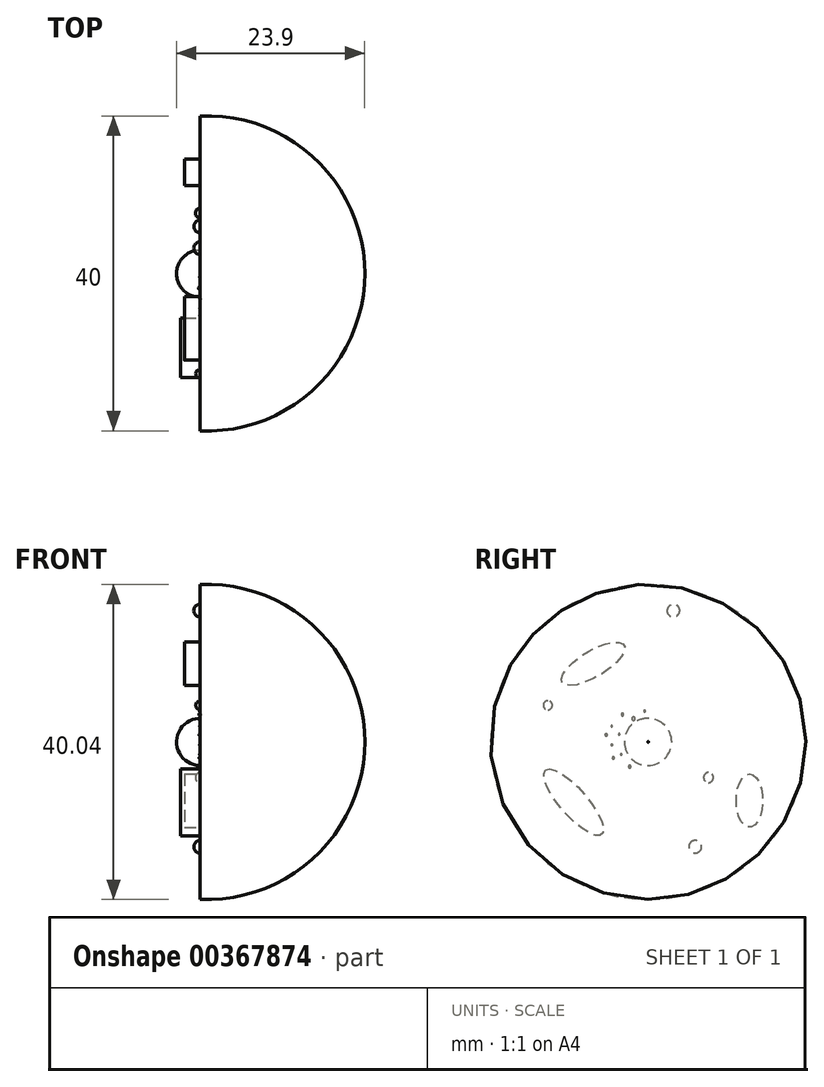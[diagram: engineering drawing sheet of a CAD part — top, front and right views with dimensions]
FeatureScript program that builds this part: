
annotation { "Feature Type Name" : "Feature", "Feature Type Description" : "" }
export const myFeature = defineFeature(function(context is Context, id is Id, definition is map)
    precondition{}
    {
        {
            var Q0;
            Q0=qCreatedBy(makeId("Front.planeOp"),FACE);
            var sketch = newSketch(context, id + "F0", { "sketchPlane" : qUnion([Q0])});
            skLineSegment(sketch, "E0", {"start": v(0, 0) * mm, "end": v(0, 20) * mm});
            skLineSegment(sketch, "E1", {"start": v(0, 0) * mm, "end": v(20.9, 0) * mm});
            skArc(sketch, "E2", {"start": v(20.9, 0) * mm, "mid": v(14.71, 14.46) * mm, "end": v(0, 20) * mm});
            skSolve(sketch);
        }
        {
            var Q0;
            Q0=makeQuery(id+"F0.imprint","IMPRINT",FACE,{"disambiguationData":[TD([[makeQuery(id+"F0.imprint","IMPRINT",EDGE,{"derivedFrom":sQuery(id+"F0.wireOp",EDGE,"E0")}),-1.0]])]});
            var Q1;
            Q1=sQuery(id+"F0.wireOp",EDGE,"E1");
            revolve(context, id + "F1", {"entities" : qUnion([Q0]), "axis" : qUnion([Q1]), "revolveType" : RevolveType.FULL});
        }
        {
            var Q0;
            Q0=qCreatedBy(makeId("Right.planeOp"),FACE);
            var sketch = newSketch(context, id + "F2", { "sketchPlane" : qUnion([Q0])});
            skLineSegment(sketch, "E3", {"start": v(0, 0) * mm, "end": v(0, 3) * mm});
            skLineSegment(sketch, "E4", {"start": v(0, 0) * mm, "end": v(-3, 0) * mm});
            skArc(sketch, "E5", {"start": v(0, 3) * mm, "mid": v(-2.14, 2.14) * mm, "end": v(-3, 0) * mm});
            skSolve(sketch);
        }
        {
            var Q0;
            Q0 = qSketchRegion(id + "F2", true);
            var Q1;
            Q1=sQuery(id+"F2.wireOp",EDGE,"E4");
            revolve(context, id + "F3", {"operationType" : NewBodyOperationType.ADD, "entities" : qUnion([Q0]), "axis" : qUnion([Q1]), "revolveType" : RevolveType.FULL});
        }
        {
            var Q0;
            Q0=makeQuery(id+"F1.opRevolve","SWEPT_FACE",FACE,{"disambiguationData":[OSD([sQuery(id+"F0.wireOp",EDGE,"E0")])]});
            var sketch = newSketch(context, id + "F4", { "sketchPlane" : qUnion([Q0])});
            skLineSegment(sketch, "E6", {"start": v(0, 0) * mm, "end": v(-3, 0) * mm});
            skLineSegment(sketch, "E7", {"start": v(0, 0) * mm, "end": v(0, 3) * mm});
            skArc(sketch, "E8", {"start": v(0, 3) * mm, "mid": v(-2.1, 2.1) * mm, "end": v(-3, 0) * mm});
            skSolve(sketch);
        }
        {
            var Q0;
            Q0=makeQuery(id+"F4.imprint","IMPRINT",FACE,{"disambiguationData":[TD([[makeQuery(id+"F4.imprint","IMPRINT",EDGE,{"derivedFrom":sQuery(id+"F4.wireOp",EDGE,"E6")}),-1.0]])]});
            var Q1;
            Q1=sQuery(id+"F4.wireOp",EDGE,"E6");
            revolve(context, id + "F5", {"operationType" : NewBodyOperationType.ADD, "entities" : qUnion([Q0]), "axis" : qUnion([Q1]), "revolveType" : RevolveType.FULL});
        }
        {
            var Q0;
            Q0=makeQuery(id+"F1.opRevolve","SWEPT_FACE",FACE,{"disambiguationData":[OSD([sQuery(id+"F0.wireOp",EDGE,"E0")])]});
            var sketch = newSketch(context, id + "F6", { "sketchPlane" : qUnion([Q0])});
            skEllipse(sketch, "E9", {"center": v(9.46, -7.67) * mm, "majorRadius": 5.42 * mm, "minorRadius": 1.7 * mm, "majorAxis": v(0.66, 0.75)});
            skSolve(sketch);
        }
        {
            var Q0;
            Q0 = qSketchRegion(id + "F6", true);
            extrude(context, id + "F7", {"entities" : qUnion([Q0]), "depth" : 2.5 * mm});
        }
        {
            var Q0;
            Q0=makeQuery(id+"F7.opExtrude","CAP_FACE",FACE,{"disambiguationData":[OSD([sQuery(id+"F6.wireOp",EDGE,"E9")])],"isStart":false});
            var sketch = newSketch(context, id + "F8", { "sketchPlane" : qUnion([Q0])});
            skFitSpline(sketch, "E10", {"points": [v(7.97, -11.28) * mm, v(6.8, -8.9) * mm, v(9.38, -10.19) * mm, v(8.17, -7.24) * mm, v(11, -8.49) * mm, v(9.27, -5.4) * mm, v(11.92, -6.7) * mm, v(11.05, -4) * mm, v(13.1, -5.01) * mm], "startDerivative": vector(-20.7, 30.85) * mm, "endDerivative": vector(27.66, -19.9) * mm});
            skSolve(sketch);
        }
        {
            var Q0;
            Q0 = qSketchRegion(id + "F8", true);
            var Q1;
            Q1=sQuery(id+"F8.wireOp",EDGE,"E10");
            extrude(context, id + "F9", {"entities" : qUnion([Q0]), "bodyType" : ToolBodyType.SURFACE, "surfaceEntities" : qUnion([Q1]), "oppositeDirection" : true, "depth" : 2 * mm});
        }
        {
            var Q0;
            Q0=makeQuery(id+"F1.opRevolve","SWEPT_FACE",FACE,{"disambiguationData":[OSD([sQuery(id+"F0.wireOp",EDGE,"E0")])]});
            var sketch = newSketch(context, id + "F10", { "sketchPlane" : qUnion([Q0])});
            skSolve(sketch);
        }
        {
            var Q0;
            {var subQ1=sQuery(id+"F0.wireOp",EDGE,"E0");Q0=makeQuery(id+"F10.imprint","IMPRINT",FACE,{"disambiguationData":[TD([[makeQuery(id+"F10.imprint","IMPRINT",EDGE,{"derivedFrom":makeQuery(id+"F1.opRevolve","SWEPT_EDGE",EDGE,{"disambiguationData":[OSD([subQ1,sQuery(id+"F0.wireOp",EDGE,"E2")])]})}),1.0]])]});}
            var sketch = newSketch(context, id + "F11", { "sketchPlane" : qUnion([Q0])});
            skSolve(sketch);
        }
        {
            var Q0;
            {var subQ1=sQuery(id+"F0.wireOp",EDGE,"E0");Q0=makeQuery(id+"F10.imprint","IMPRINT",FACE,{"disambiguationData":[TD([[makeQuery(id+"F10.imprint","IMPRINT",EDGE,{"derivedFrom":makeQuery(id+"F1.opRevolve","SWEPT_EDGE",EDGE,{"disambiguationData":[OSD([subQ1,sQuery(id+"F0.wireOp",EDGE,"E2")])]})}),1.0]])]});}
            var sketch = newSketch(context, id + "F12", { "sketchPlane" : qUnion([Q0])});
            skEllipse(sketch, "E11", {"center": v(6.98, 9.93) * mm, "majorRadius": 4.6 * mm, "minorRadius": 1.66 * mm, "majorAxis": v(0.86, -0.51)});
            skSolve(sketch);
        }
        {
            var Q0;
            Q0 = qSketchRegion(id + "F12", true);
            extrude(context, id + "F13", {"entities" : qUnion([Q0]), "depth" : 2 * mm});
        }
        {
            var Q0;
            Q0=makeQuery(id+"F13.opExtrude","CAP_FACE",FACE,{"disambiguationData":[OSD([sQuery(id+"F12.wireOp",EDGE,"E11")])],"isStart":false});
            var sketch = newSketch(context, id + "F14", { "sketchPlane" : qUnion([Q0])});
            skFitSpline(sketch, "E12", {"points": [v(4.68, 12.63) * mm, v(3.63, 10.54) * mm, v(6.2, 12.18) * mm, v(5.11, 9.18) * mm, v(7.84, 11.35) * mm, v(6.92, 8.06) * mm, v(9.45, 10.2) * mm, v(9.08, 7.26) * mm], "startDerivative": vector(-17.32, -26.87) * mm, "endDerivative": vector(-10.03, -33.63) * mm});
            skSolve(sketch);
        }
        {
            var Q0;
            Q0 = qSketchRegion(id + "F14", true);
            var Q1;
            Q1=sQuery(id+"F14.wireOp",EDGE,"E12");
            extrude(context, id + "F15", {"entities" : qUnion([Q0]), "bodyType" : ToolBodyType.SURFACE, "surfaceEntities" : qUnion([Q1]), "oppositeDirection" : true, "depth" : 2 * mm});
        }
        {
            var Q0;
            {var subQ1=sQuery(id+"F0.wireOp",EDGE,"E0");Q0=makeQuery(id+"F10.imprint","IMPRINT",FACE,{"disambiguationData":[TD([[makeQuery(id+"F10.imprint","IMPRINT",EDGE,{"derivedFrom":makeQuery(id+"F1.opRevolve","SWEPT_EDGE",EDGE,{"disambiguationData":[OSD([subQ1,sQuery(id+"F0.wireOp",EDGE,"E2")])]})}),1.0]])]});}
            var sketch = newSketch(context, id + "F16", { "sketchPlane" : qUnion([Q0])});
            skFitSpline(sketch, "E13", {"points": [v(-13.4, 3.83) * mm, v(-13, 6.76) * mm, v(-11.02, 11.05) * mm, v(-7.06, 13.56) * mm, v(-3.83, 13.87) * mm, v(-2.72, 12.84) * mm, v(-4.78, 12.22) * mm, v(-7.76, 11.16) * mm, v(-9.8, 9.35) * mm, v(-10.94, 6.79) * mm, v(-11.41, 3.75) * mm, v(-10.83, 2.72) * mm, v(-9.4, 6.15) * mm, v(-7.32, 9.32) * mm, v(-3.78, 10.86) * mm, v(-3.25, 8.93) * mm, v(-5.3, 8.35) * mm, v(-7.26, 6.9) * mm, v(-8.35, 4.25) * mm, v(-7.57, 3.02) * mm, v(-6.48, 4.95) * mm, v(-5.4, 6.65) * mm, v(-2.94, 7.46) * mm, v(-2.5, 6.23) * mm, v(-4.8, 5.59) * mm, v(-6.14, 2.41) * mm], "startDerivative": vector(4.96, 65.1) * mm, "endDerivative": vector(-14.45, -88.75) * mm});
            skSolve(sketch);
        }
        {
            var Q0;
            Q0 = qSketchRegion(id + "F16", true);
            var Q1;
            Q1=sQuery(id+"F16.wireOp",EDGE,"E13");
            extrude(context, id + "F17", {"entities" : qUnion([Q0]), "bodyType" : ToolBodyType.SURFACE, "surfaceEntities" : qUnion([Q1]), "depth" : 2 * mm});
        }
        {
            var Q0;
            {var subQ1=sQuery(id+"F0.wireOp",EDGE,"E0");Q0=makeQuery(id+"F10.imprint","IMPRINT",FACE,{"disambiguationData":[TD([[makeQuery(id+"F10.imprint","IMPRINT",EDGE,{"derivedFrom":makeQuery(id+"F1.opRevolve","SWEPT_EDGE",EDGE,{"disambiguationData":[OSD([subQ1,sQuery(id+"F0.wireOp",EDGE,"E2")])]})}),1.0]])]});}
            var sketch = newSketch(context, id + "F18", { "sketchPlane" : qUnion([Q0])});
            skFitSpline(sketch, "E14", {"points": [v(1.63, 7.11) * mm, v(4.78, 6.86) * mm, v(8.1, 5.2) * mm, v(9.66, 1.11) * mm, v(8.41, -3.01) * mm, v(4.67, -6.66) * mm, v(1.55, -7.21) * mm, v(1.07, -5.9) * mm, v(5.1, -4.45) * mm, v(7.63, -0.85) * mm, v(7.17, 3.33) * mm, v(4.59, 5.28) * mm, v(0, 5.94) * mm, v(0, 5.08) * mm, v(3.24, 4.42) * mm, v(5.82, 2.74) * mm, v(6.18, 0) * mm, v(5.56, -2.02) * mm, v(3.12, -3.79) * mm, v(1.15, -4.12) * mm, v(1.1, -3.42) * mm, v(3.12, -2.7) * mm, v(4.9, -0.76) * mm, v(4.7, 2.17) * mm, v(3.65, 3.54) * mm, v(1.42, 3.89) * mm, v(0, 3.94) * mm, v(0, 3.36) * mm, v(2.32, 3.19) * mm, v(3.68, 1.68) * mm, v(3.9, 0) * mm, v(3.27, -1.54) * mm, v(2.16, -2.36) * mm], "startDerivative": vector(88.94, -1.16) * mm, "endDerivative": vector(-52.62, -29.6) * mm});
            skSolve(sketch);
        }
        {
            var Q0;
            Q0 = qSketchRegion(id + "F18", true);
            var Q1;
            Q1=sQuery(id+"F18.wireOp",EDGE,"E14");
            extrude(context, id + "F19", {"entities" : qUnion([Q0]), "bodyType" : ToolBodyType.SURFACE, "surfaceEntities" : qUnion([Q1]), "depth" : 1.8 * mm});
        }
        {
            var Q0;
            {var subQ1=sQuery(id+"F0.wireOp",EDGE,"E0");Q0=makeQuery(id+"F10.imprint","IMPRINT",FACE,{"disambiguationData":[TD([[makeQuery(id+"F10.imprint","IMPRINT",EDGE,{"derivedFrom":makeQuery(id+"F1.opRevolve","SWEPT_EDGE",EDGE,{"disambiguationData":[OSD([subQ1,sQuery(id+"F0.wireOp",EDGE,"E2")])]})}),1.0]])]});}
            var sketch = newSketch(context, id + "F20", { "sketchPlane" : qUnion([Q0])});
            skLineSegment(sketch, "E15", {"start": v(-7.66, -5.18) * mm, "end": v(-7.66, -3.88) * mm});
            skArc(sketch, "E16", {"start": v(-7.66, -3.88) * mm, "mid": v(-8.27, -4.53) * mm, "end": v(-7.66, -5.18) * mm});
            skSolve(sketch);
        }
        {
            var Q0;
            Q0 = qSketchRegion(id + "F20", true);
            var Q1;
            Q1=sQuery(id+"F20.wireOp",EDGE,"E15");
            revolve(context, id + "F21", {"operationType" : NewBodyOperationType.ADD, "entities" : qUnion([Q0]), "axis" : qUnion([Q1]), "revolveType" : RevolveType.FULL});
        }
        {
            var Q0;
            {var subQ1=sQuery(id+"F0.wireOp",EDGE,"E0");Q0=makeQuery(id+"F10.imprint","IMPRINT",FACE,{"disambiguationData":[TD([[makeQuery(id+"F10.imprint","IMPRINT",EDGE,{"derivedFrom":makeQuery(id+"F1.opRevolve","SWEPT_EDGE",EDGE,{"disambiguationData":[OSD([subQ1,sQuery(id+"F0.wireOp",EDGE,"E2")])]})}),1.0]])]});}
            var sketch = newSketch(context, id + "F22", { "sketchPlane" : qUnion([Q0])});
            skLineSegment(sketch, "E17", {"start": v(12.74, 4.08) * mm, "end": v(12.74, 5.23) * mm});
            skArc(sketch, "E18", {"start": v(12.74, 5.23) * mm, "mid": v(12.17, 4.66) * mm, "end": v(12.74, 4.08) * mm});
            skSolve(sketch);
        }
        {
            var Q0;
            Q0 = qSketchRegion(id + "F22", true);
            var Q1;
            Q1=sQuery(id+"F22.wireOp",EDGE,"E17");
            revolve(context, id + "F23", {"operationType" : NewBodyOperationType.ADD, "entities" : qUnion([Q0]), "axis" : qUnion([Q1]), "revolveType" : RevolveType.FULL});
        }
        {
            var Q0;
            {var subQ1=sQuery(id+"F0.wireOp",EDGE,"E0");Q0=makeQuery(id+"F10.imprint","IMPRINT",FACE,{"disambiguationData":[TD([[makeQuery(id+"F10.imprint","IMPRINT",EDGE,{"derivedFrom":makeQuery(id+"F1.opRevolve","SWEPT_EDGE",EDGE,{"disambiguationData":[OSD([subQ1,sQuery(id+"F0.wireOp",EDGE,"E2")])]})}),1.0]])]});}
            var sketch = newSketch(context, id + "F24", { "sketchPlane" : qUnion([Q0])});
            skLineSegment(sketch, "E19", {"start": v(-5.97, -14.13) * mm, "end": v(-5.97, -12.52) * mm});
            skArc(sketch, "E20", {"start": v(-5.97, -12.52) * mm, "mid": v(-6.78, -13.33) * mm, "end": v(-5.97, -14.13) * mm});
            skSolve(sketch);
        }
        {
            var Q0;
            Q0 = qSketchRegion(id + "F24", true);
            var Q1;
            Q1=sQuery(id+"F24.wireOp",EDGE,"E19");
            revolve(context, id + "F25", {"operationType" : NewBodyOperationType.ADD, "entities" : qUnion([Q0]), "axis" : qUnion([Q1]), "revolveType" : RevolveType.FULL});
        }
        {
            var Q0;
            {var subQ1=sQuery(id+"F0.wireOp",EDGE,"E0");Q0=makeQuery(id+"F10.imprint","IMPRINT",FACE,{"disambiguationData":[TD([[makeQuery(id+"F10.imprint","IMPRINT",EDGE,{"derivedFrom":makeQuery(id+"F1.opRevolve","SWEPT_EDGE",EDGE,{"disambiguationData":[OSD([subQ1,sQuery(id+"F0.wireOp",EDGE,"E2")])]})}),1.0]])]});}
            var sketch = newSketch(context, id + "F26", { "sketchPlane" : qUnion([Q0])});
            skLineSegment(sketch, "E21", {"start": v(-3.75, 16.1) * mm, "end": v(-2.67, 17.25) * mm});
            skArc(sketch, "E22", {"start": v(-2.67, 17.25) * mm, "mid": v(-3.8, 17.24) * mm, "end": v(-3.75, 16.1) * mm});
            skSolve(sketch);
        }
        {
            var Q0;
            Q0 = qSketchRegion(id + "F26", true);
            var Q1;
            Q1=sQuery(id+"F26.wireOp",EDGE,"E21");
            revolve(context, id + "F27", {"operationType" : NewBodyOperationType.ADD, "entities" : qUnion([Q0]), "axis" : qUnion([Q1]), "revolveType" : RevolveType.FULL});
        }
        {
            var Q0;
            {var subQ1=sQuery(id+"F0.wireOp",EDGE,"E0");Q0=makeQuery(id+"F10.imprint","IMPRINT",FACE,{"disambiguationData":[TD([[makeQuery(id+"F10.imprint","IMPRINT",EDGE,{"derivedFrom":makeQuery(id+"F1.opRevolve","SWEPT_EDGE",EDGE,{"disambiguationData":[OSD([subQ1,sQuery(id+"F0.wireOp",EDGE,"E2")])]})}),1.0]])]});}
            var sketch = newSketch(context, id + "F28", { "sketchPlane" : qUnion([Q0])});
            skLineSegment(sketch, "E23", {"start": v(3.12, 3.49) * mm, "end": v(3.4, 3.49) * mm});
            skArc(sketch, "E24", {"start": v(3.4, 3.49) * mm, "mid": v(3.26, 3.61) * mm, "end": v(3.12, 3.49) * mm});
            skSolve(sketch);
        }
        {
            var Q0;
            Q0 = qSketchRegion(id + "F28", true);
            var Q1;
            Q1=sQuery(id+"F28.wireOp",EDGE,"E23");
            revolve(context, id + "F29", {"entities" : qUnion([Q0]), "axis" : qUnion([Q1]), "revolveType" : RevolveType.FULL});
        }
        {
            var Q0;
            {var subQ1=sQuery(id+"F0.wireOp",EDGE,"E0");Q0=makeQuery(id+"F10.imprint","IMPRINT",FACE,{"disambiguationData":[TD([[makeQuery(id+"F10.imprint","IMPRINT",EDGE,{"derivedFrom":makeQuery(id+"F1.opRevolve","SWEPT_EDGE",EDGE,{"disambiguationData":[OSD([subQ1,sQuery(id+"F0.wireOp",EDGE,"E2")])]})}),1.0]])]});}
            var sketch = newSketch(context, id + "F30", { "sketchPlane" : qUnion([Q0])});
            skLineSegment(sketch, "E25", {"start": v(1.66, 2.96) * mm, "end": v(2.07, 2.96) * mm});
            skArc(sketch, "E26", {"start": v(2.07, 2.96) * mm, "mid": v(1.86, 3.17) * mm, "end": v(1.66, 2.96) * mm});
            skSolve(sketch);
        }
        {
            var Q0;
            Q0 = qSketchRegion(id + "F30", true);
            var Q1;
            Q1=sQuery(id+"F30.wireOp",EDGE,"E25");
            revolve(context, id + "F31", {"operationType" : NewBodyOperationType.ADD, "entities" : qUnion([Q0]), "axis" : qUnion([Q1]), "revolveType" : RevolveType.FULL});
        }
        {
            var Q0;
            {var subQ1=sQuery(id+"F0.wireOp",EDGE,"E0");Q0=makeQuery(id+"F10.imprint","IMPRINT",FACE,{"disambiguationData":[TD([[makeQuery(id+"F10.imprint","IMPRINT",EDGE,{"derivedFrom":makeQuery(id+"F1.opRevolve","SWEPT_EDGE",EDGE,{"disambiguationData":[OSD([subQ1,sQuery(id+"F0.wireOp",EDGE,"E2")])]})}),1.0]])]});}
            var sketch = newSketch(context, id + "F32", { "sketchPlane" : qUnion([Q0])});
            skLineSegment(sketch, "E27", {"start": v(4.55, 2) * mm, "end": v(4.73, 2) * mm});
            skArc(sketch, "E28", {"start": v(4.73, 2) * mm, "mid": v(4.64, 2.07) * mm, "end": v(4.55, 2) * mm});
            skSolve(sketch);
        }
        {
            var Q0;
            Q0 = qSketchRegion(id + "F32", true);
            var Q1;
            Q1=sQuery(id+"F32.wireOp",EDGE,"E27");
            revolve(context, id + "F33", {"operationType" : NewBodyOperationType.ADD, "entities" : qUnion([Q0]), "axis" : qUnion([Q1]), "revolveType" : RevolveType.FULL});
        }
        {
            var Q0;
            {var subQ1=sQuery(id+"F0.wireOp",EDGE,"E0");Q0=makeQuery(id+"F10.imprint","IMPRINT",FACE,{"disambiguationData":[TD([[makeQuery(id+"F10.imprint","IMPRINT",EDGE,{"derivedFrom":makeQuery(id+"F1.opRevolve","SWEPT_EDGE",EDGE,{"disambiguationData":[OSD([subQ1,sQuery(id+"F0.wireOp",EDGE,"E2")])]})}),1.0]])]});}
            var sketch = newSketch(context, id + "F34", { "sketchPlane" : qUnion([Q0])});
            skLineSegment(sketch, "E29", {"start": v(4.5, -0.38) * mm, "end": v(4.7, -0.38) * mm});
            skArc(sketch, "E30", {"start": v(4.5, -0.38) * mm, "mid": v(4.6, -0.48) * mm, "end": v(4.7, -0.38) * mm});
            skSolve(sketch);
        }
        {
            var Q0;
            Q0 = qSketchRegion(id + "F34", true);
            var Q1;
            Q1=sQuery(id+"F34.wireOp",EDGE,"E29");
            revolve(context, id + "F35", {"operationType" : NewBodyOperationType.ADD, "entities" : qUnion([Q0]), "axis" : qUnion([Q1]), "revolveType" : RevolveType.FULL});
        }
        {
            var Q0;
            {var subQ1=sQuery(id+"F0.wireOp",EDGE,"E0");Q0=makeQuery(id+"F10.imprint","IMPRINT",FACE,{"disambiguationData":[TD([[makeQuery(id+"F10.imprint","IMPRINT",EDGE,{"derivedFrom":makeQuery(id+"F1.opRevolve","SWEPT_EDGE",EDGE,{"disambiguationData":[OSD([subQ1,sQuery(id+"F0.wireOp",EDGE,"E2")])]})}),1.0]])]});}
            var sketch = newSketch(context, id + "F36", { "sketchPlane" : qUnion([Q0])});
            skLineSegment(sketch, "E31", {"start": v(2.2, -3.15) * mm, "end": v(2.49, -3.15) * mm});
            skArc(sketch, "E32", {"start": v(2.49, -3.15) * mm, "mid": v(2.34, -3) * mm, "end": v(2.2, -3.15) * mm});
            skSolve(sketch);
        }
        {
            var Q0;
            Q0 = qSketchRegion(id + "F36", true);
            var Q1;
            Q1=sQuery(id+"F36.wireOp",EDGE,"E31");
            revolve(context, id + "F37", {"operationType" : NewBodyOperationType.ADD, "entities" : qUnion([Q0]), "axis" : qUnion([Q1]), "revolveType" : RevolveType.FULL});
        }
        {
            var Q0;
            {var subQ1=sQuery(id+"F0.wireOp",EDGE,"E0");Q0=makeQuery(id+"F10.imprint","IMPRINT",FACE,{"disambiguationData":[TD([[makeQuery(id+"F10.imprint","IMPRINT",EDGE,{"derivedFrom":makeQuery(id+"F1.opRevolve","SWEPT_EDGE",EDGE,{"disambiguationData":[OSD([subQ1,sQuery(id+"F0.wireOp",EDGE,"E2")])]})}),1.0]])]});}
            var sketch = newSketch(context, id + "F38", { "sketchPlane" : qUnion([Q0])});
            skLineSegment(sketch, "E33", {"start": v(3.6, 0.96) * mm, "end": v(3.78, 0.96) * mm});
            skArc(sketch, "E34", {"start": v(3.78, 0.96) * mm, "mid": v(3.7, 1.05) * mm, "end": v(3.6, 0.96) * mm});
            skSolve(sketch);
        }
        {
            var Q0;
            Q0 = qSketchRegion(id + "F38", true);
            var Q1;
            Q1=sQuery(id+"F38.wireOp",EDGE,"E33");
            revolve(context, id + "F39", {"operationType" : NewBodyOperationType.ADD, "entities" : qUnion([Q0]), "axis" : qUnion([Q1]), "revolveType" : RevolveType.FULL});
        }
        {
            var Q0;
            {var subQ1=sQuery(id+"F0.wireOp",EDGE,"E0");Q0=makeQuery(id+"F10.imprint","IMPRINT",FACE,{"disambiguationData":[TD([[makeQuery(id+"F10.imprint","IMPRINT",EDGE,{"derivedFrom":makeQuery(id+"F1.opRevolve","SWEPT_EDGE",EDGE,{"disambiguationData":[OSD([subQ1,sQuery(id+"F0.wireOp",EDGE,"E2")])]})}),1.0]])]});}
            var sketch = newSketch(context, id + "F40", { "sketchPlane" : qUnion([Q0])});
            skLineSegment(sketch, "E35", {"start": v(0.35, 3.91) * mm, "end": v(0.56, 3.91) * mm});
            skArc(sketch, "E36", {"start": v(0.56, 3.91) * mm, "mid": v(0.46, 4.02) * mm, "end": v(0.35, 3.91) * mm});
            skSolve(sketch);
        }
        {
            var Q0;
            Q0 = qSketchRegion(id + "F40", true);
            var Q1;
            Q1=sQuery(id+"F40.wireOp",EDGE,"E35");
            revolve(context, id + "F41", {"operationType" : NewBodyOperationType.ADD, "entities" : qUnion([Q0]), "axis" : qUnion([Q1]), "revolveType" : RevolveType.FULL});
        }
        {
            var Q0;
            {var subQ1=sQuery(id+"F0.wireOp",EDGE,"E0");Q0=makeQuery(id+"F10.imprint","IMPRINT",FACE,{"disambiguationData":[TD([[makeQuery(id+"F10.imprint","IMPRINT",EDGE,{"derivedFrom":makeQuery(id+"F1.opRevolve","SWEPT_EDGE",EDGE,{"disambiguationData":[OSD([subQ1,sQuery(id+"F0.wireOp",EDGE,"E2")])]})}),1.0]])]});}
            var sketch = newSketch(context, id + "F42", { "sketchPlane" : qUnion([Q0])});
            skLineSegment(sketch, "E37", {"start": v(5.24, 1) * mm, "end": v(5.43, 0.8) * mm});
            skArc(sketch, "E38", {"start": v(5.43, 0.8) * mm, "mid": v(5.44, 1) * mm, "end": v(5.24, 1) * mm});
            skSolve(sketch);
        }
        {
            var Q0;
            Q0 = qSketchRegion(id + "F42", true);
            var Q1;
            Q1=sQuery(id+"F42.wireOp",EDGE,"E37");
            revolve(context, id + "F43", {"operationType" : NewBodyOperationType.ADD, "entities" : qUnion([Q0]), "axis" : qUnion([Q1]), "revolveType" : RevolveType.FULL});
        }
        {
            var Q0;
            {var subQ1=sQuery(id+"F0.wireOp",EDGE,"E0");Q0=makeQuery(id+"F11.imprint","IMPRINT",FACE,{"disambiguationData":[TD([[makeQuery(id+"F11.imprint","IMPRINT",EDGE,{"derivedFrom":makeQuery(id+"F10.imprint","IMPRINT",EDGE,{"derivedFrom":makeQuery(id+"F1.opRevolve","SWEPT_EDGE",EDGE,{"disambiguationData":[OSD([subQ1,sQuery(id+"F0.wireOp",EDGE,"E2")])]})})}),1.0]])]});}
            var sketch = newSketch(context, id + "F44", { "sketchPlane" : qUnion([Q0])});
            skLineSegment(sketch, "E39", {"start": v(4.34, -2.15) * mm, "end": v(4.53, -1.94) * mm});
            skArc(sketch, "E40", {"start": v(4.53, -1.94) * mm, "mid": v(4.33, -1.95) * mm, "end": v(4.34, -2.15) * mm});
            skSolve(sketch);
        }
        {
            var Q0;
            Q0 = qSketchRegion(id + "F44", true);
            var Q1;
            Q1=sQuery(id+"F44.wireOp",EDGE,"E39");
            revolve(context, id + "F45", {"operationType" : NewBodyOperationType.ADD, "entities" : qUnion([Q0]), "axis" : qUnion([Q1]), "revolveType" : RevolveType.FULL});
        }
        {
            var Q0;
            {var subQ1=sQuery(id+"F0.wireOp",EDGE,"E0");Q0=makeQuery(id+"F11.imprint","IMPRINT",FACE,{"disambiguationData":[TD([[makeQuery(id+"F11.imprint","IMPRINT",EDGE,{"derivedFrom":makeQuery(id+"F10.imprint","IMPRINT",EDGE,{"derivedFrom":makeQuery(id+"F1.opRevolve","SWEPT_EDGE",EDGE,{"disambiguationData":[OSD([subQ1,sQuery(id+"F0.wireOp",EDGE,"E2")])]})})}),1.0]])]});}
            var sketch = newSketch(context, id + "F46", { "sketchPlane" : qUnion([Q0])});
            skLineSegment(sketch, "E41", {"start": v(3.35, -1.58) * mm, "end": v(3.52, -1.58) * mm});
            skArc(sketch, "E42", {"start": v(3.35, -1.58) * mm, "mid": v(3.43, -1.67) * mm, "end": v(3.52, -1.58) * mm});
            skSolve(sketch);
        }
        {
            var Q0;
            Q0 = qSketchRegion(id + "F46", true);
            var Q1;
            Q1=sQuery(id+"F46.wireOp",EDGE,"E41");
            revolve(context, id + "F47", {"operationType" : NewBodyOperationType.ADD, "entities" : qUnion([Q0]), "axis" : qUnion([Q1]), "revolveType" : RevolveType.FULL});
        }
        {
            var Q0;
            {var subQ1=sQuery(id+"F0.wireOp",EDGE,"E0");Q0=makeQuery(id+"F11.imprint","IMPRINT",FACE,{"disambiguationData":[TD([[makeQuery(id+"F11.imprint","IMPRINT",EDGE,{"derivedFrom":makeQuery(id+"F10.imprint","IMPRINT",EDGE,{"derivedFrom":makeQuery(id+"F1.opRevolve","SWEPT_EDGE",EDGE,{"disambiguationData":[OSD([subQ1,sQuery(id+"F0.wireOp",EDGE,"E2")])]})})}),1.0]])]});}
            var sketch = newSketch(context, id + "F48", { "sketchPlane" : qUnion([Q0])});
            skEllipse(sketch, "E43", {"center": v(-12.87, -7.45) * mm, "majorRadius": 3.4 * mm, "minorRadius": 1.69 * mm, "majorAxis": v(0, 1)});
            skSolve(sketch);
        }
        {
            var Q0;
            Q0 = qSketchRegion(id + "F48", true);
            extrude(context, id + "F49", {"entities" : qUnion([Q0]), "depth" : 2 * mm});
        }
    });
